# Revit family: Fabrisorb Panels - Square
name_source: partatom
category: Generic Models
revit_build: Autodesk Revit 2016 (Build: 20150220_1215(x64)
units: mm (PartAtom-declared; Revit-internal decimal feet)

## family parameters
Always vertical = No
Can host rebar = No
Cut with Voids When Loaded = No
Part Type = Normal
Room Calculation Point = No
Round Connector Dimension = Use Diameter
Shared = No
Work Plane-Based = Yes

## types (6) — shared parameters
Default Elevation = 4' - 0"
Finish = Guilford of Maine Anchorage or FR701 Acoustic Fabric
Manufacturer = Acoustical Surfaces, Inc.
Material = Fabrisorb
URL = https://www.acousticalsurfaces.com

## per-type parameters (varying)
| type | A | Length | Thickness | Width |
| 2 INCH THICK - 48X96 | 0' - 1" | 8' - 0" | 0' - 2" | 4' - 0" |
| 2 INCH THICK - 24X48 | 0' - 1" | 4' - 0" | 0' - 2" | 2' - 0" |
| 2 INCH THICK - 24X24 | 0' - 1" | 2' - 0" | 0' - 2" | 2' - 0" |
| 1 INCH THICK - 48X96 | 0' - 0 1/2" | 8' - 0" | 0' - 1" | 4' - 0" |
| 1 INCH THICK - 24X48 | 0' - 0 1/2" | 4' - 0" | 0' - 1" | 2' - 0" |
| 1 INCH THICK - 24X24 | 0' - 0 1/2" | 2' - 0" | 0' - 1" | 2' - 0" |

## geometry (parser evidence)
native form markers: Sweep x2
no freeform markers — native parametric forms only
